# Revit family: MLS3-DI
name_source: partatom
category: Lighting Fixtures
units: mm (PartAtom-declared; Revit-internal decimal feet)

## family parameters
Cut with Voids When Loaded = No
Host = Face
Light Source = Yes
OmniClass Number = 23.80.70.11
OmniClass Title = Luminaries for Internal Lighting
Part Type = Normal
Room Calculation Point = No
Round Connector Dimension = Use Diameter
Shared = No

## types (1)
- MLS3-DI
    Apparent Load = 0 VA
    Color Filter = 16777215
    Dimming Lamp Color Temperature Shift = <None>
    Emit Shape Visible in Rendering = No
    Emit from Rectangle Length = 4' - 0"
    Emit from Rectangle Width = 2' - 0"
    Fixture width = 0' - 3"
    Housing = Metal, Paint Finish, White, Matte
    Lamp = LED
    Lens = Acrylic
    Load Classifcation = Lighting
    Manufacturer = Mercury Lighting
    Model = MLS3-DI
    Photometric Web File = MLS3-DI-48-550-850-35K-ASO-BW-1-2C-U-LLIA001503-011.ies
    Tilt Angle = 90.00°
    URL = https://mercltg.com
    Voltage Comment = 120/277 UNV Volt

## geometry (parser evidence)
native form markers: Extrusion x1, Sweep x5
no freeform markers — native parametric forms only
